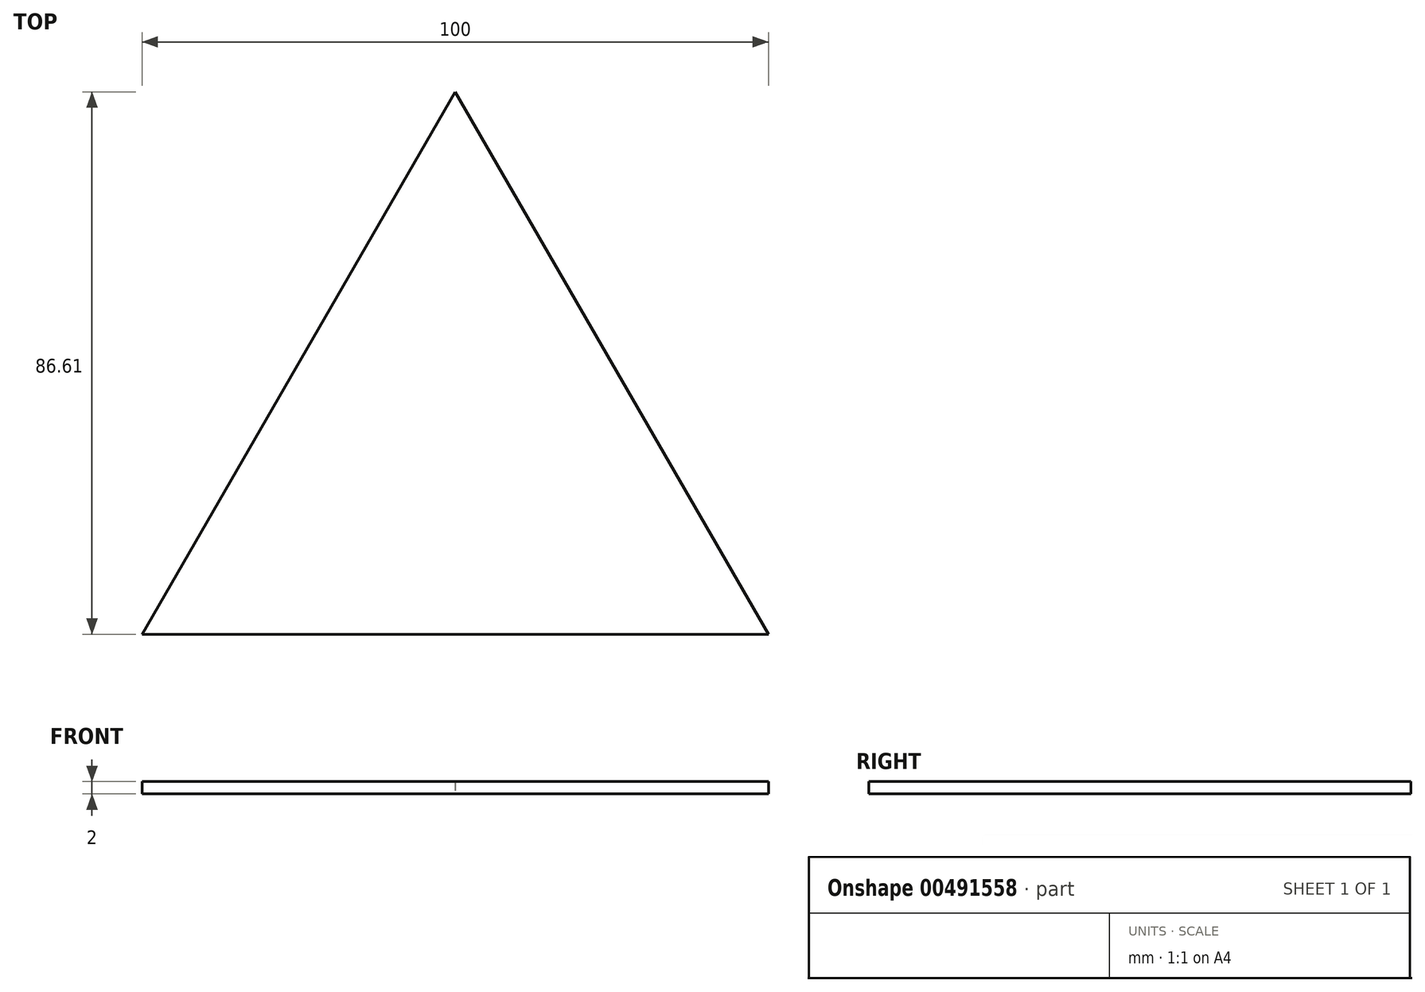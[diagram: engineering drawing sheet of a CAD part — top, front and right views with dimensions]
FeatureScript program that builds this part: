
annotation { "Feature Type Name" : "Feature", "Feature Type Description" : "" }
export const myFeature = defineFeature(function(context is Context, id is Id, definition is map)
    precondition{}
    {
        {
            var Q0;
            Q0=qCreatedBy(makeId("Top.planeOp"),FACE);
            var sketch = newSketch(context, id + "F0", { "sketchPlane" : qUnion([Q0])});
            skLineSegment(sketch, "E0", {"start": v(-50, -28.87) * mm, "end": v(50, -28.87) * mm});
            skLineSegment(sketch, "E1", {"start": v(-50, -28.87) * mm, "end": v(0, 57.74) * mm});
            skLineSegment(sketch, "E2", {"start": v(0, 57.74) * mm, "end": v(50, -28.87) * mm});
            skLineSegment(sketch, "E3", {"start": v(-25, 14.43) * mm, "end": v(50, -28.87) * mm, "construction": true});
            skLineSegment(sketch, "E4", {"start": v(-50, -28.87) * mm, "end": v(25, 14.43) * mm, "construction": true});
            skLineSegment(sketch, "E5", {"start": v(0, -28.87) * mm, "end": v(0, 0) * mm});
            skLineSegment(sketch, "E6", {"start": v(0, 57.74) * mm, "end": v(-16.67, 28.87) * mm, "construction": true});
            skLineSegment(sketch, "E7", {"start": v(-50, -28.87) * mm, "end": v(-33.33, 0) * mm, "construction": true});
            skLineSegment(sketch, "E8.MirrorCS", {"start": v(0, 57.74) * mm, "end": v(16.67, 28.87) * mm, "construction": true});
            skLineSegment(sketch, "E9.MirrorCS", {"start": v(50, -28.87) * mm, "end": v(33.33, 0) * mm, "construction": true});
            skLineSegment(sketch, "E10", {"start": v(-50, -28.87) * mm, "end": v(-16.67, -28.87) * mm, "construction": true});
            skLineSegment(sketch, "E11.MirrorCS", {"start": v(50, -28.87) * mm, "end": v(16.67, -28.87) * mm, "construction": true});
            skLineSegment(sketch, "E12", {"start": v(-16.67, 28.87) * mm, "end": v(16.67, 28.87) * mm, "construction": true});
            skLineSegment(sketch, "E13", {"start": v(-33.33, 0) * mm, "end": v(33.33, 0) * mm, "construction": true});
            skLineSegment(sketch, "E14", {"start": v(-33.33, 0) * mm, "end": v(-16.67, -28.87) * mm, "construction": true});
            skLineSegment(sketch, "E15", {"start": v(16.67, -28.87) * mm, "end": v(33.33, 0) * mm, "construction": true});
            skLineSegment(sketch, "E16", {"start": v(-16.67, 28.87) * mm, "end": v(0, 0) * mm, "construction": true});
            skLineSegment(sketch, "E17", {"start": v(0, 0) * mm, "end": v(16.67, 28.87) * mm, "construction": true});
            skLineSegment(sketch, "E18", {"start": v(-16.67, -28.87) * mm, "end": v(0, 0) * mm, "construction": true});
            skLineSegment(sketch, "E19", {"start": v(0, 0) * mm, "end": v(16.67, -28.87) * mm, "construction": true});
            skSolve(sketch);
        }
        {
            var Q0;
            {var subQ0=sQuery(id+"F0.wireOp",EDGE,"E1");Q0=makeQuery(id+"F0.imprint","IMPRINT",FACE,{"disambiguationData":[TD([[makeQuery(id+"F0.imprint","IMPRINT",EDGE,{"derivedFrom":subQ0}),-1.0]])]});}
            extrude(context, id + "F1", {"entities" : qUnion([Q0]), "depth" : 2 * mm, "offsetDistance" : 25 * mm});
        }
    });
